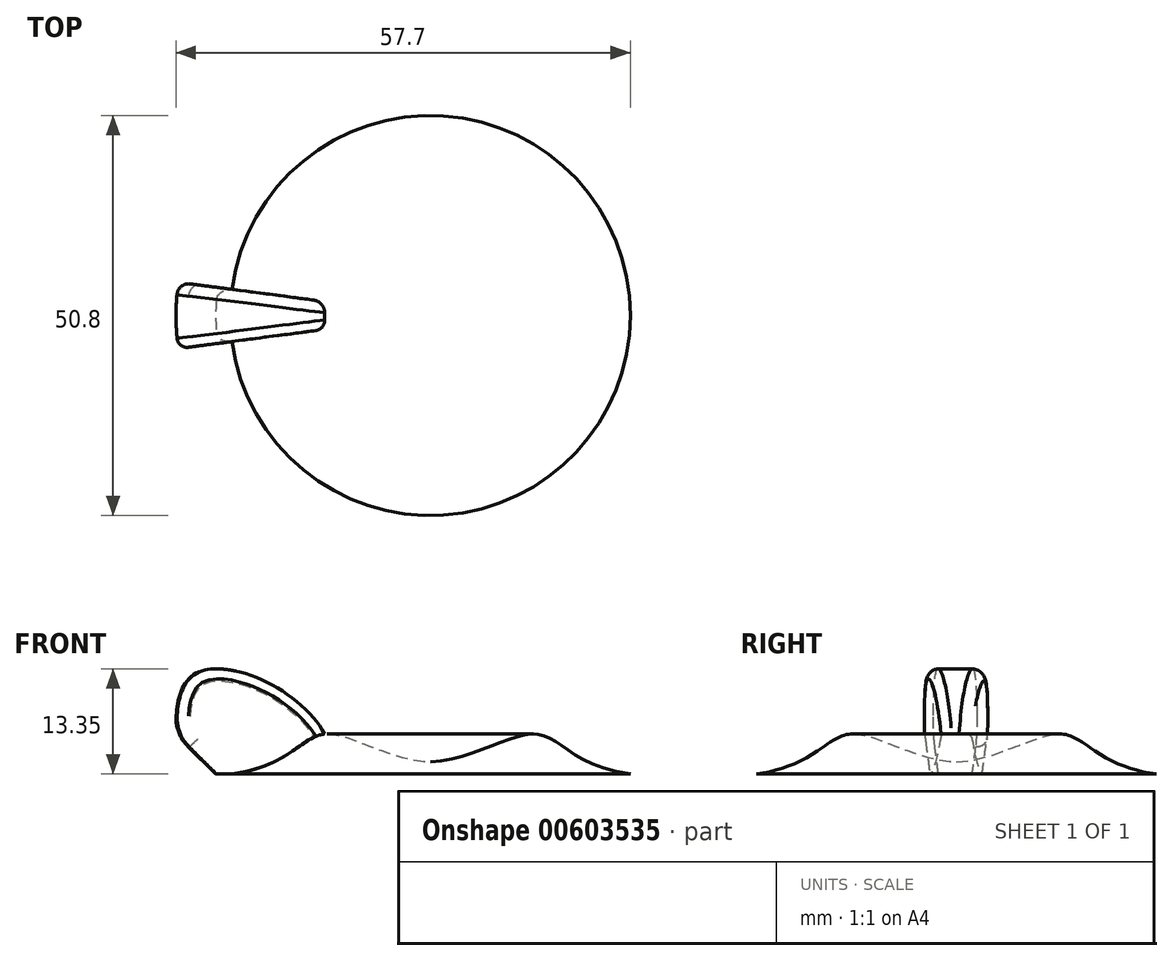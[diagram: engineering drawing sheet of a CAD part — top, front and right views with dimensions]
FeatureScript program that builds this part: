
annotation { "Feature Type Name" : "Feature", "Feature Type Description" : "" }
export const myFeature = defineFeature(function(context is Context, id is Id, definition is map)
    precondition{}
    {
        {
            var Q0;
            Q0=qCreatedBy(makeId("Front.planeOp"),FACE);
            var sketch = newSketch(context, id + "F0", { "sketchPlane" : qUnion([Q0])});
            skLineSegment(sketch, "E0", {"start": v(0, 0) * mm, "end": v(25.4, 0) * mm});
            skLineSegment(sketch, "E1", {"start": v(0, 0) * mm, "end": v(0, 1.52) * mm});
            skFitSpline(sketch, "E2", {"points": [v(0, 1.52) * mm, v(13.45, 5.08) * mm, v(25.4, 0) * mm], "startDerivative": vector(32.15, 1.45) * mm, "endDerivative": vector(45.48, -6.3) * mm});
            skSolve(sketch);
        }
        {
            var Q0;
            Q0=makeQuery(id+"F0.imprint","IMPRINT",FACE,{"disambiguationData":[TD([[makeQuery(id+"F0.imprint","IMPRINT",EDGE,{"derivedFrom":sQuery(id+"F0.wireOp",EDGE,"E0")}),1.0]])]});
            var Q1;
            Q1=sQuery(id+"F0.wireOp",EDGE,"E1");
            revolve(context, id + "F1", {"entities" : qUnion([Q0]), "axis" : qUnion([Q1]), "revolveType" : RevolveType.FULL});
        }
        {
            var Q0;
            Q0=qCreatedBy(makeId("Front.planeOp"),FACE);
            var sketch = newSketch(context, id + "F2", { "sketchPlane" : qUnion([Q0])});
            skLineSegment(sketch, "E3", {"start": v(-12, 0) * mm, "end": v(-32.31, 0) * mm});
            skLineSegment(sketch, "E4", {"start": v(-32.31, 0) * mm, "end": v(-32.31, 3.82) * mm});
            skFitSpline(sketch, "E5", {"points": [v(-32.31, 3.82) * mm, v(-29.42, 12.97) * mm, v(-12, 0) * mm], "startDerivative": vector(-0.51, 23.07) * mm, "endDerivative": vector(0.69, -45.3) * mm});
            skLineSegment(sketch, "E6", {"start": v(0, 21.42) * mm, "end": v(0, 47.37) * mm, "construction": true});
            skSolve(sketch);
        }
        {
            var Q0;
            Q0=makeQuery(id+"F2.imprint","IMPRINT",FACE,{"disambiguationData":[TD([[makeQuery(id+"F2.imprint","IMPRINT",EDGE,{"derivedFrom":sQuery(id+"F2.wireOp",EDGE,"E3")}),-1.0]])]});
            var Q1;
            Q1=sQuery(id+"F2.wireOp",EDGE,"E6");
            revolve(context, id + "F3", {"operationType" : NewBodyOperationType.ADD, "entities" : qUnion([Q0]), "axis" : qUnion([Q1]), "revolveType" : RevolveType.SYMMETRIC, "angle" : 15 * degree});
        }
        {
            var Q0;
            Q0=makeQuery(id+"F3.opRevolve","SWEPT_EDGE",EDGE,{"disambiguationData":[OSD([sQuery(id+"F2.wireOp",EDGE,"E3"),sQuery(id+"F2.wireOp",EDGE,"E4")])]});
            chamfer(context, id + "F4", {"entities" : qUnion([Q0]), "width" : 5.08 * mm, "tangentPropagation" : true});
        }
        {
            var Q0;
            Q0=makeQuery(id+"F4.opChamfer","BLEND_EDGE",EDGE,{"blendedFrom":[makeQuery(id+"F3.opRevolve","SWEPT_EDGE",EDGE,{"disambiguationData":[OSD([sQuery(id+"F2.wireOp",EDGE,"E3"),sQuery(id+"F2.wireOp",EDGE,"E4")])]}),makeQuery(id+"F3.opRevolve","SWEPT_FACE",FACE,{"disambiguationData":[OSD([sQuery(id+"F2.wireOp",EDGE,"E5")])]})],"blendedInto":[makeQuery(id+"F3.opRevolve","SWEPT_FACE",FACE,{"disambiguationData":[OSD([sQuery(id+"F2.wireOp",EDGE,"E5")])]})]});
            fillet(context, id + "F5", {"entities" : qUnion([Q0]), "radius" : 5.08 * mm, "tangentPropagation" : true, "allowEdgeOverflow" : false});
        }
        {
            var Q0;
            Q0=makeQuery(id+"F3.opRevolve","CAP_EDGE",EDGE,{"disambiguationData":[OSD([sQuery(id+"F2.wireOp",EDGE,"E5")])],"isStart":true});
            var Q1;
            {var subQ0=sQuery(id+"F2.wireOp",EDGE,"E5");var subQ1=sQuery(id+"F2.wireOp",EDGE,"E4");var subQ2=sQuery(id+"F2.wireOp",EDGE,"E3");Q1=makeQuery(id+"F5.opFillet","BLEND_EDGE",EDGE,{"blendedFrom":[makeQuery(id+"F4.opChamfer","BLEND_EDGE",EDGE,{"blendedFrom":[makeQuery(id+"F3.opRevolve","SWEPT_EDGE",EDGE,{"disambiguationData":[OSD([subQ2,subQ1])]}),makeQuery(id+"F3.opRevolve","SWEPT_FACE",FACE,{"disambiguationData":[OSD([subQ0])]})],"blendedInto":[makeQuery(id+"F3.opRevolve","SWEPT_FACE",FACE,{"disambiguationData":[OSD([subQ0])]})]}),makeQuery(id+"F3.opRevolve","CAP_FACE",FACE,{"disambiguationData":[OSD([subQ2,subQ1,subQ0])],"isStart":true})],"blendedInto":[makeQuery(id+"F3.opRevolve","CAP_FACE",FACE,{"disambiguationData":[OSD([subQ2,subQ1,subQ0])],"isStart":true})]});}
            fillet(context, id + "F6", {"entities" : qUnion([Q0, Q1]), "radius" : 1.52 * mm, "tangentPropagation" : true, "allowEdgeOverflow" : false});
        }
        {
            var Q0;
            Q0=makeQuery(id+"F3.opRevolve","CAP_EDGE",EDGE,{"disambiguationData":[OSD([sQuery(id+"F2.wireOp",EDGE,"E5")])],"isStart":false});
            var Q1;
            {var subQ0=sQuery(id+"F2.wireOp",EDGE,"E5");var subQ1=sQuery(id+"F2.wireOp",EDGE,"E4");var subQ2=sQuery(id+"F2.wireOp",EDGE,"E3");Q1=makeQuery(id+"F5.opFillet","BLEND_EDGE",EDGE,{"blendedFrom":[makeQuery(id+"F4.opChamfer","BLEND_EDGE",EDGE,{"blendedFrom":[makeQuery(id+"F3.opRevolve","SWEPT_EDGE",EDGE,{"disambiguationData":[OSD([subQ2,subQ1])]}),makeQuery(id+"F3.opRevolve","SWEPT_FACE",FACE,{"disambiguationData":[OSD([subQ0])]})],"blendedInto":[makeQuery(id+"F3.opRevolve","SWEPT_FACE",FACE,{"disambiguationData":[OSD([subQ0])]})]}),makeQuery(id+"F3.opRevolve","CAP_FACE",FACE,{"disambiguationData":[OSD([subQ2,subQ1,subQ0])],"isStart":false})],"blendedInto":[makeQuery(id+"F3.opRevolve","CAP_FACE",FACE,{"disambiguationData":[OSD([subQ2,subQ1,subQ0])],"isStart":false})]});}
            fillet(context, id + "F7", {"entities" : qUnion([Q0, Q1]), "radius" : 1.27 * mm, "tangentPropagation" : true, "allowEdgeOverflow" : false});
        }
    });
